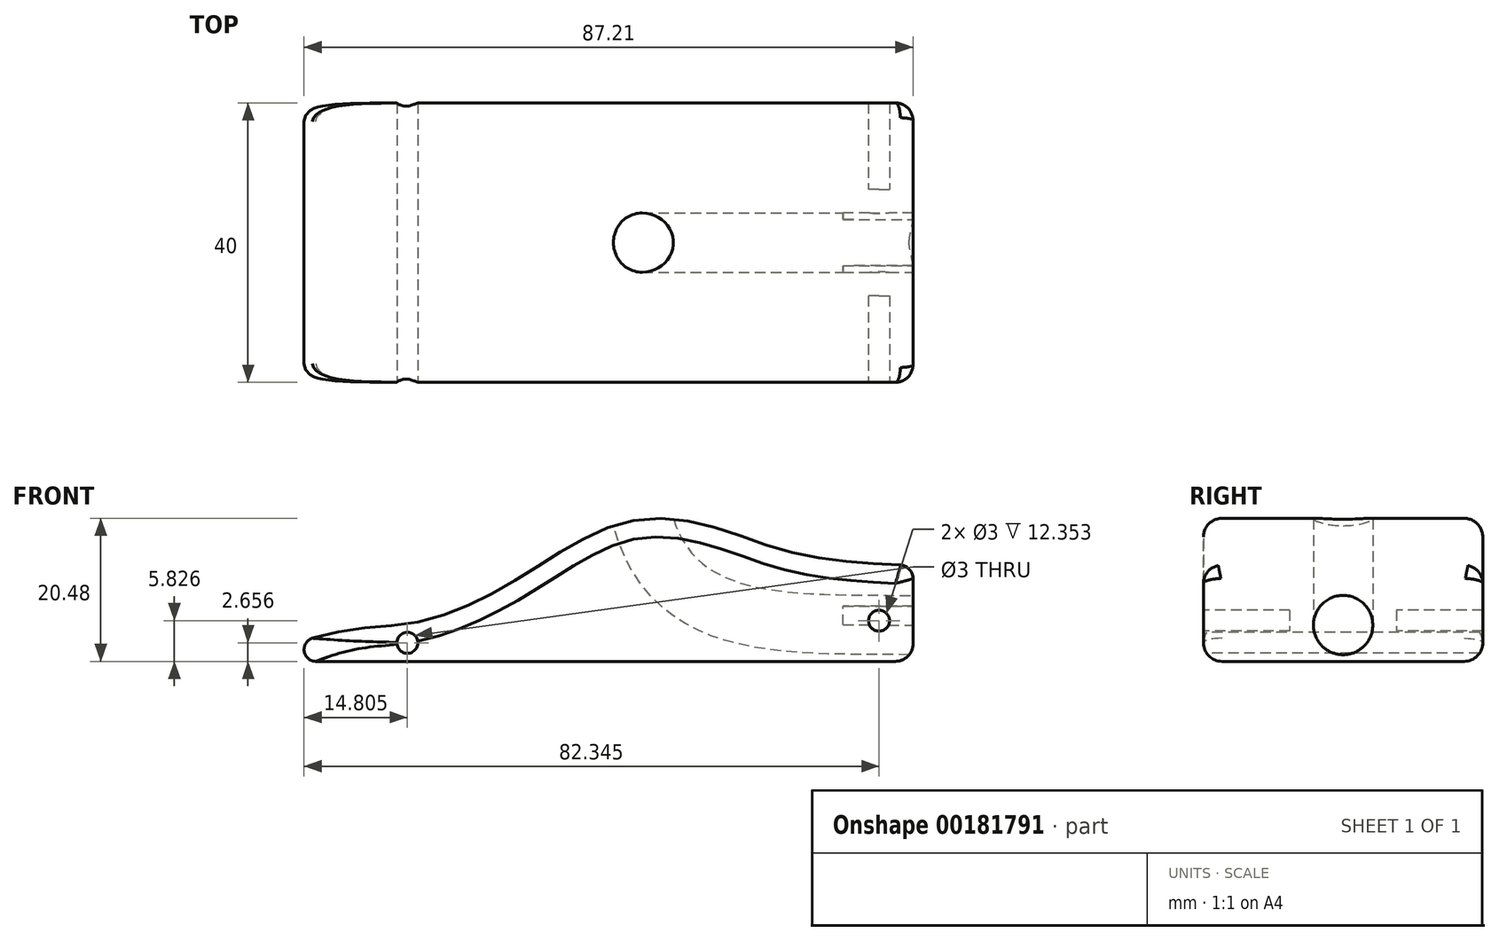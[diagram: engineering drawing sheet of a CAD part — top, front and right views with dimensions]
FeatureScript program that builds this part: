
annotation { "Feature Type Name" : "Feature", "Feature Type Description" : "" }
export const myFeature = defineFeature(function(context is Context, id is Id, definition is map)
    precondition{}
    {
        {
            var Q0;
            Q0=qCreatedBy(makeId("Front.planeOp"),FACE);
            var sketch = newSketch(context, id + "F0", { "sketchPlane" : qUnion([Q0])});
            skFitSpline(sketch, "E0", {"points": [v(-94.74, 0) * mm, v(-72, 5.4) * mm, v(-57.23, 11.43) * mm, v(-40.07, 20.19) * mm, v(-24.8, 18.01) * mm, v(0, 13.72) * mm], "startDerivative": vector(181.07, 80.63) * mm, "endDerivative": vector(210.38, -7.22) * mm});
            skLineSegment(sketch, "E1", {"start": v(0, 13.72) * mm, "end": v(0, 0) * mm});
            skLineSegment(sketch, "E2", {"start": v(0, 0) * mm, "end": v(-94.74, 0) * mm});
            skSolve(sketch);
        }
        {
            var Q0;
            Q0 = qSketchRegion(id + "F0", true);
            extrude(context, id + "F1", {"entities" : qUnion([Q0]), "endBound" : BoundingType.SYMMETRIC, "depth" : 40 * mm});
        }
        {
            var Q0;
            Q0=makeQuery(id+"F1.opExtrude","SWEPT_EDGE",EDGE,{"disambiguationData":[OSD([sQuery(id+"F0.wireOp",EDGE,"E0"),sQuery(id+"F0.wireOp",EDGE,"E2")])]});
            fillet(context, id + "F2", {"entities" : qUnion([Q0]), "radius" : 1.69 * mm, "tangentPropagation" : true, "allowEdgeOverflow" : false});
        }
        {
            var Q0;
            Q0=makeQuery(id+"F1.opExtrude","CAP_EDGE",EDGE,{"disambiguationData":[OSD([sQuery(id+"F0.wireOp",EDGE,"E0")])],"isStart":false});
            var Q1;
            Q1=makeQuery(id+"F1.opExtrude","CAP_EDGE",EDGE,{"disambiguationData":[OSD([sQuery(id+"F0.wireOp",EDGE,"E0")])],"isStart":true});
            fillet(context, id + "F3", {"entities" : qUnion([Q0, Q1]), "radius" : 2.66 * mm, "tangentPropagation" : true, "allowEdgeOverflow" : false});
        }
        {
            var Q0;
            Q0=makeQuery(id+"F1.opExtrude","SWEPT_EDGE",EDGE,{"disambiguationData":[OSD([sQuery(id+"F0.wireOp",EDGE,"E0"),sQuery(id+"F0.wireOp",EDGE,"E1")])]});
            fillet(context, id + "F4", {"entities" : qUnion([Q0]), "radius" : 1.89 * mm, "allowEdgeOverflow" : false});
        }
        {
            var Q0;
            {var subQ0=sQuery(id+"F0.wireOp",EDGE,"E0");Q0=makeQuery(id+"F4.opFillet","BLEND_EDGE",EDGE,{"blendedFrom":[makeQuery(id+"F1.opExtrude","SWEPT_EDGE",EDGE,{"disambiguationData":[OSD([subQ0,sQuery(id+"F0.wireOp",EDGE,"E1")])]}),makeQuery(id+"F3.opFillet","BLEND_FACE",FACE,{"disambiguationData":[OSD([subQ0]),TDD([makeQuery(id+"F1.opExtrude","CAP_EDGE",EDGE,{"disambiguationData":[OSD([subQ0])],"isStart":false})])]})],"blendedInto":[makeQuery(id+"F3.opFillet","BLEND_FACE",FACE,{"disambiguationData":[OSD([subQ0]),TDD([makeQuery(id+"F1.opExtrude","CAP_EDGE",EDGE,{"disambiguationData":[OSD([subQ0])],"isStart":false})])]})]});}
            var Q1;
            {var subQ0=sQuery(id+"F0.wireOp",EDGE,"E0");Q1=makeQuery(id+"F4.opFillet","BLEND_EDGE",EDGE,{"blendedFrom":[makeQuery(id+"F1.opExtrude","SWEPT_EDGE",EDGE,{"disambiguationData":[OSD([subQ0,sQuery(id+"F0.wireOp",EDGE,"E1")])]}),makeQuery(id+"F3.opFillet","BLEND_FACE",FACE,{"disambiguationData":[OSD([subQ0]),TDD([makeQuery(id+"F1.opExtrude","CAP_EDGE",EDGE,{"disambiguationData":[OSD([subQ0])],"isStart":true})])]})],"blendedInto":[makeQuery(id+"F3.opFillet","BLEND_FACE",FACE,{"disambiguationData":[OSD([subQ0]),TDD([makeQuery(id+"F1.opExtrude","CAP_EDGE",EDGE,{"disambiguationData":[OSD([subQ0])],"isStart":true})])]})]});}
            fillet(context, id + "F5", {"entities" : qUnion([Q0, Q1]), "radius" : 2.5 * mm, "tangentPropagation" : true, "allowEdgeOverflow" : false});
        }
        {
            var Q0;
            Q0=qCreatedBy(makeId("Front.planeOp"),FACE);
            var sketch = newSketch(context, id + "F6", { "sketchPlane" : qUnion([Q0])});
            skFitSpline(sketch, "E3", {"points": [v(0, 6.2) * mm, v(-38.88, 27.68) * mm], "startDerivative": vector(-64.14, 0.54) * mm, "endDerivative": vector(-4.33, 67.65) * mm});
            skSolve(sketch);
        }
        {
            var Q0;
            Q0=qCreatedBy(makeId("Right.planeOp"),FACE);
            var sketch = newSketch(context, id + "F7", { "sketchPlane" : qUnion([Q0])});
            skCircle(sketch, "E4", {"center": v(0, 5.2) * mm, "radius": 4.25 * mm});
            skSolve(sketch);
        }
        {
            var Q0;
            Q0 = qSketchRegion(id + "F7", true);
            var Q1;
            Q1 = qConstructionFilter(qBodyType(qCreatedBy(id + "F6" ,EDGE), BodyType.WIRE), ConstructionObject.NO);
            sweep(context, id + "F8", {"operationType" : NewBodyOperationType.REMOVE, "profiles" : qUnion([Q0]), "path" : qUnion([Q1])});
        }
        {
            var Q0;
            Q0=makeQuery(id+"F1.opExtrude","CAP_FACE",FACE,{"disambiguationData":[OSD([sQuery(id+"F0.wireOp",EDGE,"E0"),sQuery(id+"F0.wireOp",EDGE,"E1"),sQuery(id+"F0.wireOp",EDGE,"E2")])],"isStart":false});
            var sketch = newSketch(context, id + "F9", { "sketchPlane" : qUnion([Q0])});
            skPoint(sketch, "E5", {"position": v(-4.86, 5.83) * mm});
            skPoint(sketch, "E6", {"position": v(-72.4, 2.66) * mm});
            skSolve(sketch);
        }
        {
            var Q0;
            Q0=sQuery(id+"F9.wireOp",VERTEX,"E6");
            var Q1;
            Q1=sQuery(id+"F9.wireOp",VERTEX,"E5");
            var Q2;
            Q2=makeQuery(id+"F1.opExtrude","SWEPT_BODY",BODY,{"disambiguationData":[OSD([sQuery(id+"F0.wireOp",EDGE,"E0"),sQuery(id+"F0.wireOp",EDGE,"E1"),sQuery(id+"F0.wireOp",EDGE,"E2")])]});
            hole(context, id + "F10", {"style" : HoleStyle.SIMPLE, "endStyle" : HoleEndStyle.THROUGH, "holeDiameter" : 3 * mm, "locations" : qUnion([Q0, Q1]), "scope" : qUnion([Q2]), "isTappedThrough" : true});
        }
        {
            var Q0;
            Q0=makeQuery(id+"F1.opExtrude","SWEPT_FACE",FACE,{"disambiguationData":[OSD([sQuery(id+"F0.wireOp",EDGE,"E1")])]});
            var sketch = newSketch(context, id + "F11", { "sketchPlane" : qUnion([Q0])});
            skArc(sketch, "E7", {"start": v(3.29, 2.5) * mm, "mid": v(4.25, 5.2) * mm, "end": v(3.29, 7.89) * mm});
            skLineSegment(sketch, "E8.bottom", {"start": v(7.65, 2.5) * mm, "end": v(3.29, 2.5) * mm});
            skLineSegment(sketch, "E8.top", {"start": v(7.65, 7.89) * mm, "end": v(3.29, 7.89) * mm});
            skLineSegment(sketch, "E8.left", {"start": v(7.65, 2.5) * mm, "end": v(7.65, 7.89) * mm});
            skLineSegment(sketch, "E8.right", {"start": v(-7.65, 2.5) * mm, "end": v(-7.65, 7.89) * mm});
            skLineSegment(sketch, "E9.trimOffspring", {"start": v(-3.29, 2.5) * mm, "end": v(-7.65, 2.5) * mm});
            skLineSegment(sketch, "E10.trimOffspring", {"start": v(-3.29, 7.89) * mm, "end": v(-7.65, 7.89) * mm});
            skArc(sketch, "E11.trimOffspring", {"start": v(-3.29, 7.89) * mm, "mid": v(-4.25, 5.2) * mm, "end": v(-3.29, 2.5) * mm});
            skSolve(sketch);
        }
        {
            var Q0;
            Q0=makeQuery(id+"F11.imprint","IMPRINT",FACE,{"disambiguationData":[TD([[makeQuery(id+"F11.imprint","IMPRINT",EDGE,{"derivedFrom":sQuery(id+"F11.wireOp",EDGE,"E7")}),1.0]])]});
            var Q1;
            Q1=makeQuery(id+"F11.imprint","IMPRINT",FACE,{"disambiguationData":[TD([[makeQuery(id+"F11.imprint","IMPRINT",EDGE,{"derivedFrom":sQuery(id+"F11.wireOp",EDGE,"E8.right")}),-1.0]])]});
            extrude(context, id + "F12", {"entities" : qUnion([Q0, Q1]), "operationType" : NewBodyOperationType.ADD, "oppositeDirection" : true, "depth" : 10 * mm});
        }
    });
